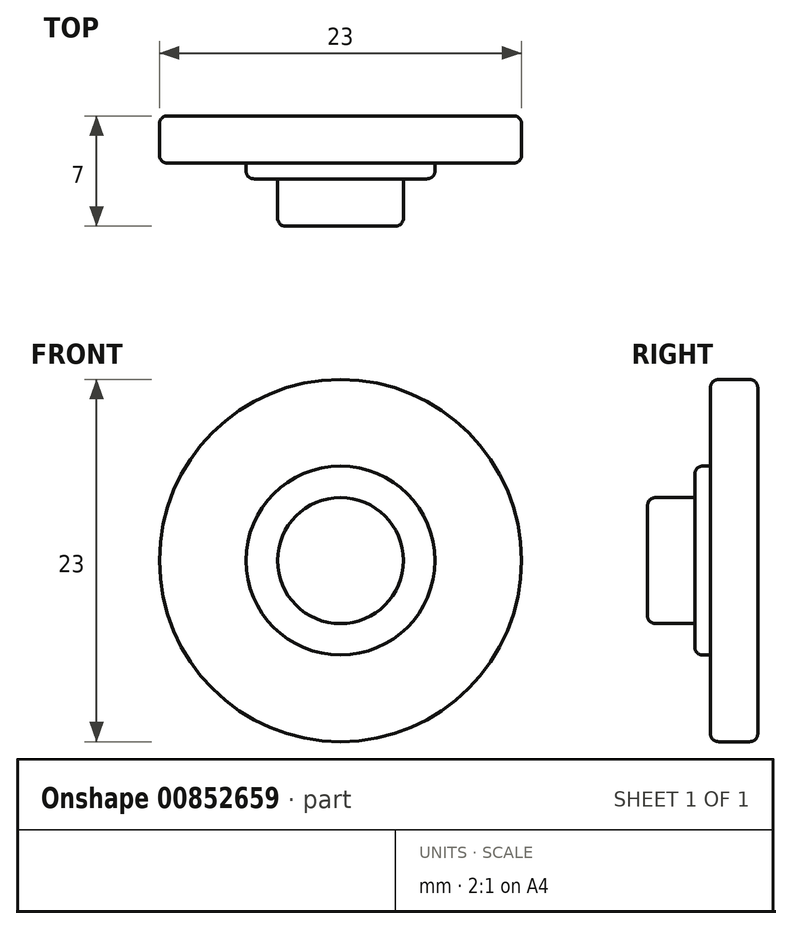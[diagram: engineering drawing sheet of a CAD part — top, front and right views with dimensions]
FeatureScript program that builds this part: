
annotation { "Feature Type Name" : "Feature", "Feature Type Description" : "" }
export const myFeature = defineFeature(function(context is Context, id is Id, definition is map)
    precondition{}
    {
        {
            var Q0;
            Q0=qCreatedBy(makeId("Front.planeOp"),FACE);
            var sketch = newSketch(context, id + "F0", { "sketchPlane" : qUnion([Q0])});
            skCircle(sketch, "E0", {"center": v(0, 0) * mm, "radius": 11.5 * mm});
            skSolve(sketch);
        }
        {
            var Q0;
            Q0=makeQuery(id+"F0.imprint","IMPRINT",FACE,{"disambiguationData":[TD([[makeQuery(id+"F0.imprint","IMPRINT",EDGE,{"derivedFrom":sQuery(id+"F0.wireOp",EDGE,"E0")}),1.0]])]});
            extrude(context, id + "F1", {"entities" : qUnion([Q0]), "depth" : 3 * mm, "offsetDistance" : 25 * mm});
        }
        {
            var Q0;
            Q0=makeQuery(id+"F1.opExtrude","CAP_FACE",FACE,{"disambiguationData":[OSD([sQuery(id+"F0.wireOp",EDGE,"E0")])],"isStart":false});
            var sketch = newSketch(context, id + "F2", { "sketchPlane" : qUnion([Q0])});
            skCircle(sketch, "E1", {"center": v(0, 0) * mm, "radius": 6 * mm});
            skSolve(sketch);
        }
        {
            var Q0;
            Q0=makeQuery(id+"F2.imprint","IMPRINT",FACE,{"disambiguationData":[TD([[makeQuery(id+"F2.imprint","IMPRINT",EDGE,{"derivedFrom":sQuery(id+"F2.wireOp",EDGE,"E1")}),1.0]])]});
            extrude(context, id + "F3", {"entities" : qUnion([Q0]), "operationType" : NewBodyOperationType.ADD, "depth" : 1 * mm, "offsetDistance" : 25 * mm});
        }
        {
            var Q0;
            Q0=makeQuery(id+"F3.opExtrude","CAP_FACE",FACE,{"disambiguationData":[OSD([sQuery(id+"F2.wireOp",EDGE,"E1")])],"isStart":false});
            var sketch = newSketch(context, id + "F4", { "sketchPlane" : qUnion([Q0])});
            skCircle(sketch, "E2", {"center": v(0, 0) * mm, "radius": 4 * mm});
            skSolve(sketch);
        }
        {
            var Q0;
            Q0=makeQuery(id+"F4.imprint","IMPRINT",FACE,{"disambiguationData":[TD([[makeQuery(id+"F4.imprint","IMPRINT",EDGE,{"derivedFrom":sQuery(id+"F4.wireOp",EDGE,"E2")}),1.0]])]});
            extrude(context, id + "F5", {"entities" : qUnion([Q0]), "operationType" : NewBodyOperationType.ADD, "depth" : 3 * mm, "offsetDistance" : 25 * mm});
        }
        {
            var Q0;
            Q0=makeQuery(id+"F1.opExtrude","CAP_EDGE",EDGE,{"disambiguationData":[OSD([sQuery(id+"F0.wireOp",EDGE,"E0")])],"isStart":true});
            var Q1;
            Q1=makeQuery(id+"F1.opExtrude","CAP_EDGE",EDGE,{"disambiguationData":[OSD([sQuery(id+"F0.wireOp",EDGE,"E0")])],"isStart":false});
            var Q2;
            Q2=makeQuery(id+"F3.opExtrude","CAP_EDGE",EDGE,{"disambiguationData":[OSD([sQuery(id+"F2.wireOp",EDGE,"E1")])],"isStart":false});
            var Q3;
            Q3=makeQuery(id+"F5.opExtrude","CAP_EDGE",EDGE,{"disambiguationData":[OSD([sQuery(id+"F4.wireOp",EDGE,"E2")])],"isStart":false});
            fillet(context, id + "F6", {"entities" : qUnion([Q0, Q1, Q2, Q3]), "radius" : 0.5 * mm, "tangentPropagation" : true, "allowEdgeOverflow" : false});
        }
    });
